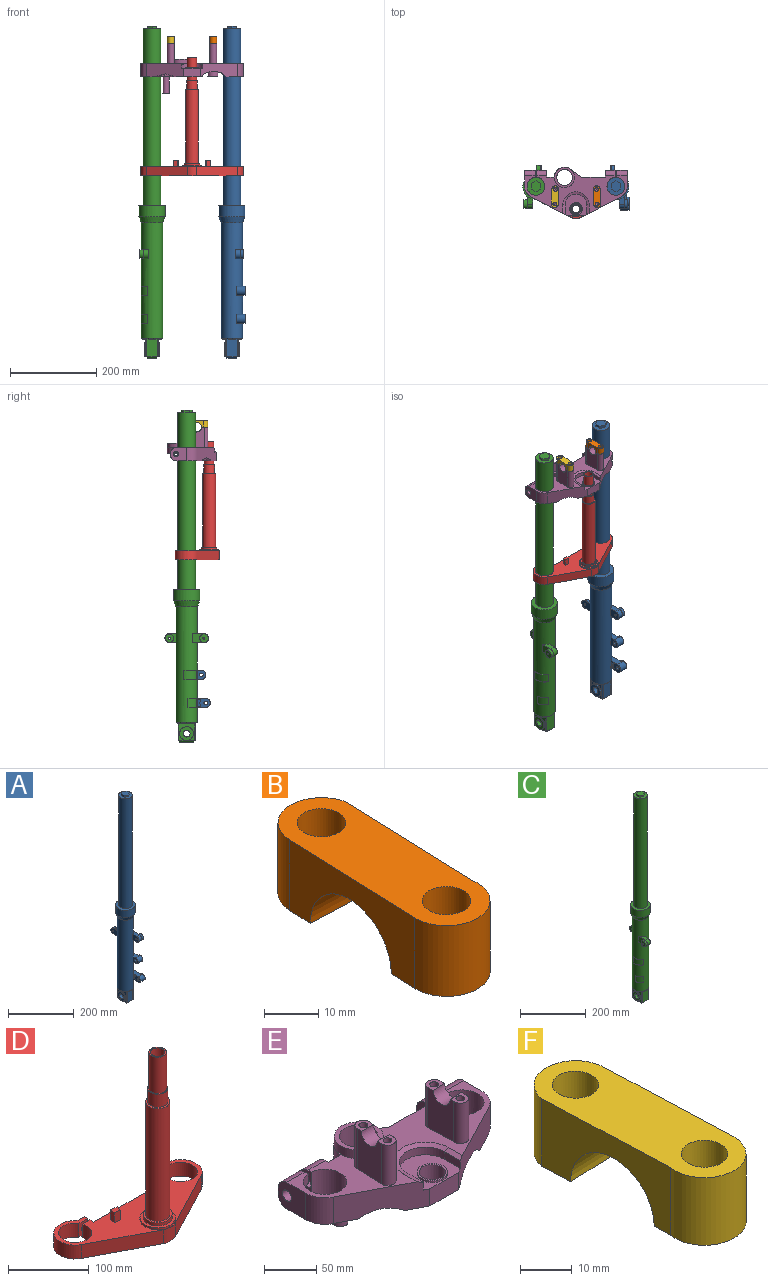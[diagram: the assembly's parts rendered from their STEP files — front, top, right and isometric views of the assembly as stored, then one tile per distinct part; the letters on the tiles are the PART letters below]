
ASSEMBLY  parts=6 mates=5
PART A: 81 faces, bbox 60.9x105.3x769.3 mm
  f0: cylinder r=10.5mm len=21mm, axis (1,0,0), area 824.7mm2, adj f15,f17,f32,f78,f80
  f1: cylinder r=10.5mm len=21mm, axis (1,0,0), area 824.7mm2, adj f2,f27,f29,f30,f46
  f2: plane 21x21mm, normal (1,0,0), area 291.3mm2, adj f1,f3
  f3: cylinder r=4.19mm len=20mm, axis (1,0,0), area 526.3mm2, adj f2,f30
  f4: cylinder r=2.46mm len=10.25mm, axis (-1,0,0), area 158.3mm2, adj f5,f6
  f5: plane 19x19mm, normal (1,0,0), area 264.5mm2, adj f4,f7
  f6: plane 28.95x21mm, normal (-1,0,0), area 541.7mm2, adj f4,f8,f9,f10,f11
  f7: cylinder r=9.5mm len=19mm, axis (-1,0,0), area 447.7mm2, adj f5,f12
  f8: plane 18.45x2.75mm, normal (0,0,-1), area 48.7mm2, adj f6,f9,f11,f12
  f9: cylinder r=10.5mm len=21mm, axis (1,0,0), area 90.7mm2, adj f6,f8,f10,f12
  f10: plane 18.45x2.75mm, normal (0,0,1), area 48.7mm2, adj f6,f9,f11,f12
  f11: cylinder r=24.65mm len=267mm, axis (0,0,-1), area 39688.9mm2, adj f6,f8,f10,f12,f13,f14,f15,f16
  f12: plane 27.57x21mm, normal (1,0,0), area 248.1mm2, adj f7,f8,f9,f10,f11
  f13: cone r=1mm half-angle=45deg, axis (0,0,1), area 565.9mm2, adj f11,f18,f19,f20,f21,f22,f33,f34
  f14: plane 50.5x50.5mm, normal (0,0,-1), area 94.1mm2, adj f11,f31
  f15: plane 41.27x15mm, normal (0,0,1), area 291mm2, adj f0,f11,f16,f32,f78
  f16: plane 21x1.71mm, normal (0,1,0), area 36mm2, adj f11,f15,f17,f32
  f17: plane 41.27x15mm, normal (0,0,-1), area 291mm2, adj f0,f11,f16,f32,f78
  f18: plane 42.22x25.29mm, normal (0,1,0), area 1007.7mm2, adj f13,f19,f22,f33,f37
  f19: plane 16.58x1.65mm, normal (0,0,-1), area 18.4mm2, adj f13,f18
  f20: plane 32.15x7.15mm, normal (0,0,-1), area 159.2mm2, adj f13,f21
  f21: plane 41.54x36.07mm, normal (-1,0,0), area 638.5mm2, adj f13,f20,f22,f38,f39,f40
  f22: cylinder r=2mm len=42.52mm, axis (0,0,-1), area 131.9mm2, adj f13,f18,f21,f37,f39
  f23: plane 26.33x12.5mm, normal (0,0,1), area 256.6mm2, adj f11,f24,f26,f43
  f24: plane 36.83x21mm, normal (1,0,0), area 411.9mm2, adj f11,f23,f25,f43,f44
  f25: plane 26.33x12.5mm, normal (0,0,-1), area 256.6mm2, adj f11,f24,f26,f43
  f26: plane 27.38x21mm, normal (-1,0,0), area 508mm2, adj f11,f23,f25,f43,f45
  f27: plane 41.27x15mm, normal (0,0,1), area 431.5mm2, adj f1,f11,f28,f30,f46
  f28: plane 21x0.87mm, normal (0,1,0), area 18.3mm2, adj f11,f27,f29,f46
  f29: plane 41.27x15mm, normal (0,0,-1), area 431.5mm2, adj f1,f11,f28,f30,f46
  f30: plane 32.37x21mm, normal (-1,0,0), area 485.9mm2, adj f1,f3,f11,f27,f29,f47,f48,f49
  f31: cone r=0.36mm half-angle=20deg, axis (0,0,1), area 2548.9mm2, adj f14,f52
  f32: plane 41.27x21mm, normal (1,0,0), area 693.5mm2, adj f0,f15,f16,f17
  f33: cylinder r=2mm len=42.52mm, axis (0,0,-1), area 131.9mm2, adj f13,f18,f34,f37,f53
  f34: plane 41.54x36.07mm, normal (1,0,0), area 638.5mm2, adj f13,f33,f35,f36,f53,f54
  f35: plane 32.15x7.15mm, normal (0,0,-1), area 159.2mm2, adj f13,f34
  f36: cylinder r=2mm len=42.52mm, axis (0,0,-1), area 131.9mm2, adj f13,f34,f41,f53,f55
  f37: plane 28.09x3.26mm, normal (0,0.71,-0.71), area 109.1mm2, adj f18,f22,f33,f39,f53,f56
  f38: cylinder r=2mm len=42.52mm, axis (0,0,-1), area 131.9mm2, adj f13,f21,f39,f41,f55
  f39: plane 39.09x3.26mm, normal (-0.71,0,-0.71), area 155.8mm2, adj f21,f22,f37,f38,f55,f56
  f40: cylinder r=16mm len=32mm, axis (-1,0,0), area 301.6mm2, adj f21,f57
  f41: plane 42.22x25.29mm, normal (0,-1,0), area 1007.7mm2, adj f13,f36,f38,f42,f55
  f42: plane 16.58x1.65mm, normal (0,0,-1), area 18.4mm2, adj f13,f41
  f43: cylinder r=10.5mm len=21mm, axis (1,0,0), area 412.3mm2, adj f23,f24,f25,f26
  f44: cylinder r=10mm len=20mm, axis (-1,0,0), area 471.2mm2, adj f24,f58
  f45: cylinder r=2.5mm len=20mm, axis (-1,0,0), area 314.2mm2, adj f26,f58
  f46: plane 41.27x21mm, normal (1,0,0), area 693.5mm2, adj f1,f27,f28,f29
  f47: plane 7.65x2.5mm, normal (0,0,1), area 19.1mm2, adj f30,f48,f51,f59
  f48: cylinder r=13.5mm len=7.5mm, axis (-1,0,0), area 19.9mm2, adj f30,f47,f49,f59
  f49: cylinder r=13.5mm len=7.5mm, axis (-1,0,0), area 19.9mm2, adj f30,f48,f50,f59
  f50: plane 7.65x2.5mm, normal (0,0,-1), area 19.1mm2, adj f30,f49,f51,f59
  f51: plane 15x2.5mm, normal (0,-1,0), area 37.5mm2, adj f30,f47,f50,f59
  f52: cylinder r=30.25mm len=60.5mm, axis (0,0,1), area 4991.6mm2, adj f31,f60
  f53: plane 39.09x3.26mm, normal (0.71,0,-0.71), area 155.7mm2, adj f33,f34,f36,f37,f55,f56
  f54: cylinder r=16mm len=32mm, axis (1,0,0), area 301.6mm2, adj f34,f61
  f55: plane 28.09x3.26mm, normal (0,-0.71,-0.71), area 109.1mm2, adj f36,f38,f39,f41,f53,f56
  f56: plane 34x23mm, normal (0,0,-1), area 568.2mm2, adj f37,f39,f53,f55,f62
  f57: plane 32x32mm, normal (-1,0,0), area 603.2mm2, adj f40,f63
  f58: plane 20x20mm, normal (1,0,0), area 294.5mm2, adj f44,f45
  f59: plane 15x7.65mm, normal (-1,0,0), area 91.6mm2, adj f47,f48,f49,f50,f51
  f60: plane 60.5x60.5mm, normal (0,0,1), area 1541.6mm2, adj f52,f64
  f61: plane 32x32mm, normal (1,0,0), area 603.2mm2, adj f54,f65
  f62: cylinder r=8.25mm len=25mm, axis (0,0,-1), area 928.2mm2, adj f56,f63,f65,f66,f67
  f63: cylinder r=8mm len=16mm, axis (-1,0,0), area 595mm2, adj f57,f62,f66,f67,f69
  f64: cylinder r=20.6mm len=410mm, axis (0,0,-1), area 53067.8mm2, adj f60,f68
  f65: cylinder r=8mm len=16.58mm, axis (1,0,0), area 645.2mm2, adj f61,f62,f66,f67,f69
  f66: plane 11.46x2.31mm, normal (0,0,-1), area 13.5mm2, adj f62,f63,f65,f69
  f67: plane 11.96x2.57mm, normal (0,0,-1), area 14.6mm2, adj f62,f63,f65,f69
  f68: plane 41.2x41.2mm, normal (0,0,1), area 914mm2, adj f64,f70,f71,f72,f73,f74,f75
  f69: cylinder r=6.92mm len=43mm, axis (0,0,1), area 1844.4mm2, adj f63,f65,f66,f67,f76
  f70: plane 11x6.35mm, normal (-0.5,0.87,0), area 76.2mm2, adj f68,f71,f75,f77
  f71: plane 12.7x6mm, normal (-1,0,0), area 76.2mm2, adj f68,f70,f72,f77
  f72: plane 11x6.35mm, normal (-0.5,-0.87,0), area 76.2mm2, adj f68,f71,f73,f77
  f73: plane 11x6.35mm, normal (0.5,-0.87,0), area 76.2mm2, adj f68,f72,f74,f77
  f74: plane 12.7x6mm, normal (1,0,0), area 76.2mm2, adj f68,f73,f75,f77
  f75: plane 11x6.35mm, normal (0.5,0.87,0), area 76.2mm2, adj f68,f70,f74,f77
  f76: cone r=1.73mm half-angle=60deg, axis (0,0,-1), area 173.6mm2, adj f69
  f77: plane 25.4x22mm, normal (0,0,1), area 419.2mm2, adj f70,f71,f72,f73,f74,f75
  f78: plane 22.37x21mm, normal (-1,0,0), area 367.4mm2, adj f0,f11,f15,f17,f79
  f79: cylinder r=4.19mm len=20mm, axis (1,0,0), area 526.3mm2, adj f78,f80
  f80: plane 21x21mm, normal (1,0,0), area 291.3mm2, adj f0,f79
PART B: 10 faces, bbox 17.2x50x16 mm
  f0: cylinder r=8.03mm len=16mm, axis (0,0,-1), area 376.8mm2, adj f2,f3,f6,f7
  f1: cylinder r=8.03mm len=16.06mm, axis (0,0,-1), area 430.7mm2, adj f2,f3,f5,f7
  f2: plane 33.98x16mm, normal (1,-0.04,0), area 353.9mm2, adj f0,f1,f4,f5,f6,f7
  f3: plane 33.98x16mm, normal (-1,0.04,0), area 353.9mm2, adj f0,f1,f4,f5,f6,f7
  f4: cylinder r=11mm len=22.59mm, axis (1,-0.04,0), area 549mm2, adj f2,f3,f5,f6
  f5: plane 16.12x14.71mm, normal (0,0,-1), area 139.2mm2, adj f1,f2,f3,f4,f8
  f6: plane 16.15x13.95mm, normal (0,0,-1), area 126.8mm2, adj f0,f2,f3,f4,f9
  f7: plane 50.04x17.23mm, normal (0,0,1), area 615.6mm2, adj f0,f1,f2,f3,f8,f9
  f8: cylinder r=4.5mm len=16mm, axis (0,0,-1), area 452.4mm2, adj f5,f7
  f9: cylinder r=4.5mm len=16mm, axis (0,0,-1), area 452.4mm2, adj f6,f7
PART C: 69 faces, bbox 60.8x101.3x769.3 mm
  f0: cylinder r=2.46mm len=10.25mm, axis (-1,0,0), area 158.3mm2, adj f1,f2
  f1: plane 19x19mm, normal (-1,0,0), area 264.5mm2, adj f0,f3
  f2: plane 28.95x21mm, normal (1,0,0), area 541.7mm2, adj f0,f4,f5,f6,f68
  f3: cylinder r=9.5mm len=19mm, axis (-1,0,0), area 447.7mm2, adj f1,f7
  f4: cylinder r=10.5mm len=21mm, axis (1,0,0), area 90.7mm2, adj f2,f5,f7,f68
  f5: plane 18.45x2.75mm, normal (0,0,1), area 48.7mm2, adj f2,f4,f6,f7
  f6: cylinder r=24.65mm len=267mm, axis (0,0,1), area 39688.9mm2, adj f2,f5,f7,f8,f9,f10,f11,f12
  f7: plane 27.57x21mm, normal (-1,0,0), area 248.1mm2, adj f3,f4,f5,f6,f68
  f8: cone r=1mm half-angle=45deg, axis (0,0,1), area 565.9mm2, adj f6,f13,f14,f15,f16,f17,f27,f28
  f9: plane 50.5x50.5mm, normal (0,0,-1), area 94.1mm2, adj f6,f26
  f10: plane 30.05x14.91mm, normal (0,0,1), area 21.4mm2, adj f6,f11,f18,f65
  f11: plane 21x0.63mm, normal (0,1,0), area 13.1mm2, adj f6,f10,f12,f65
  f12: plane 30.05x14.91mm, normal (0,0,-1), area 21.4mm2, adj f6,f11,f18,f65
  f13: plane 16.58x1.65mm, normal (0,0,-1), area 18.4mm2, adj f8,f14
  f14: plane 42.22x25.29mm, normal (0,1,0), area 1007.7mm2, adj f8,f13,f15,f30,f31
  f15: cylinder r=2mm len=42.52mm, axis (0,0,1), area 131.9mm2, adj f8,f14,f16,f31,f32
  f16: plane 41.54x36.07mm, normal (1,0,0), area 638.5mm2, adj f8,f15,f17,f32,f33,f34
  f17: plane 32.15x7.15mm, normal (0,0,-1), area 159.2mm2, adj f8,f16
  f18: plane 21x0.66mm, normal (1,0,0), area 13.8mm2, adj f6,f10,f12,f65
  f19: plane 27.38x21mm, normal (1,0,0), area 508mm2, adj f6,f21,f37,f38,f67
  f20: plane 36.83x21mm, normal (-1,0,0), area 411.9mm2, adj f6,f21,f37,f39,f67
  f21: plane 26.33x12.5mm, normal (0,0,1), area 256.6mm2, adj f6,f19,f20,f37
  f22: plane 21x0.66mm, normal (1,0,0), area 13.8mm2, adj f6,f23,f25,f66
  f23: plane 20.05x14.73mm, normal (0,0,-1), area 15.3mm2, adj f6,f22,f24,f66
  f24: plane 21x0.6mm, normal (0,1,0), area 12.7mm2, adj f6,f23,f25,f66
  f25: plane 20.05x14.73mm, normal (0,0,1), area 15.3mm2, adj f6,f22,f24,f66
  f26: cone r=0.36mm half-angle=20deg, axis (0,0,1), area 2548.9mm2, adj f9,f40
  f27: cylinder r=2mm len=42.52mm, axis (0,0,1), area 131.9mm2, adj f8,f28,f36,f41,f42
  f28: plane 41.54x36.07mm, normal (-1,0,0), area 638.5mm2, adj f8,f27,f29,f30,f42,f43
  f29: plane 32.15x7.15mm, normal (0,0,-1), area 159.2mm2, adj f8,f28
  f30: cylinder r=2mm len=42.52mm, axis (0,0,1), area 131.9mm2, adj f8,f14,f28,f31,f42
  f31: plane 28.09x3.26mm, normal (0,0.71,-0.71), area 109.1mm2, adj f14,f15,f30,f32,f42,f44
  f32: plane 39.09x3.26mm, normal (0.71,0,-0.71), area 155.8mm2, adj f15,f16,f31,f33,f41,f44
  f33: cylinder r=2mm len=42.52mm, axis (0,0,1), area 131.9mm2, adj f8,f16,f32,f36,f41
  f34: cylinder r=16mm len=32mm, axis (-1,0,0), area 301.6mm2, adj f16,f45
  f35: plane 16.58x1.65mm, normal (0,0,-1), area 18.4mm2, adj f8,f36
  f36: plane 42.22x25.29mm, normal (0,-1,0), area 1007.7mm2, adj f8,f27,f33,f35,f41
  f37: cylinder r=10.5mm len=21mm, axis (1,0,0), area 412.3mm2, adj f19,f20,f21,f67
  f38: cylinder r=2.5mm len=20mm, axis (-1,0,0), area 314.2mm2, adj f19,f46
  f39: cylinder r=10mm len=20mm, axis (-1,0,0), area 471.2mm2, adj f20,f46
  f40: cylinder r=30.25mm len=60.5mm, axis (0,0,-1), area 4991.6mm2, adj f26,f47
  f41: plane 28.09x3.26mm, normal (0,-0.71,-0.71), area 109.1mm2, adj f27,f32,f33,f36,f42,f44
  f42: plane 39.09x3.26mm, normal (-0.71,0,-0.71), area 155.8mm2, adj f27,f28,f30,f31,f41,f44
  f43: cylinder r=16mm len=32mm, axis (1,0,0), area 301.6mm2, adj f28,f48
  f44: plane 34x23mm, normal (0,0,-1), area 568.2mm2, adj f31,f32,f41,f42,f49
  f45: plane 32x32mm, normal (1,0,0), area 603.2mm2, adj f34,f50
  f46: plane 20x20mm, normal (-1,0,0), area 294.5mm2, adj f38,f39
  f47: plane 60.5x60.5mm, normal (0,0,1), area 1541.6mm2, adj f40,f51
  f48: plane 32x32mm, normal (-1,0,0), area 603.2mm2, adj f43,f52
  f49: cylinder r=8.25mm len=25mm, axis (0,0,1), area 928.2mm2, adj f44,f50,f52,f53,f54
  f50: cylinder r=8mm len=16mm, axis (-1,0,0), area 595.3mm2, adj f45,f49,f53,f54,f56
  f51: cylinder r=20.6mm len=410mm, axis (0,0,1), area 53067.8mm2, adj f47,f55
  f52: cylinder r=8mm len=16.58mm, axis (1,0,0), area 645.6mm2, adj f48,f49,f53,f54,f56
  f53: plane 11.46x2.31mm, normal (0,0,-1), area 13.5mm2, adj f49,f50,f52,f56
  f54: plane 11.96x2.57mm, normal (0,0,-1), area 14.6mm2, adj f49,f50,f52,f56
  f55: plane 41.2x41.2mm, normal (0,0,1), area 914mm2, adj f51,f57,f58,f59,f60,f61,f62
  f56: cylinder r=6.92mm len=43mm, axis (0,0,-1), area 1844.4mm2, adj f50,f52,f53,f54,f63
  f57: plane 11x6.35mm, normal (0.5,0.87,0), area 76.2mm2, adj f55,f58,f62,f64
  f58: plane 12.7x6mm, normal (1,0,0), area 76.2mm2, adj f55,f57,f59,f64
  f59: plane 11x6.35mm, normal (0.5,-0.87,0), area 76.2mm2, adj f55,f58,f60,f64
  f60: plane 11x6.35mm, normal (-0.5,-0.87,0), area 76.2mm2, adj f55,f59,f61,f64
  f61: plane 12.7x6mm, normal (-1,0,0), area 76.2mm2, adj f55,f60,f62,f64
  f62: plane 11x6.35mm, normal (-0.5,0.87,0), area 76.2mm2, adj f55,f57,f61,f64
  f63: cone r=1.73mm half-angle=60deg, axis (0,0,-1), area 173.6mm2, adj f56
  f64: plane 25.4x22mm, normal (0,0,1), area 419.2mm2, adj f57,f58,f59,f60,f61,f62
  f65: cylinder r=25.25mm len=30.05mm, axis (0,0,1), area 758.5mm2, adj f10,f11,f12,f18
  f66: cylinder r=25.25mm len=21mm, axis (0,0,1), area 546.4mm2, adj f22,f23,f24,f25
  f67: plane 26.33x12.5mm, normal (0,0,-1), area 256.6mm2, adj f6,f19,f20,f37
  f68: plane 18.45x2.75mm, normal (0,0,-1), area 48.7mm2, adj f2,f4,f6,f7
PART D: 60 faces, bbox 237.9x101.4x275 mm
  f0: plane 15x7.87mm, normal (-0.98,0.18,0), area 120mm2, adj f1,f2,f3,f10
  f1: plane 11.27x9.66mm, normal (0,0,1), area 80mm2, adj f0,f2,f3,f4
  f2: plane 15x9.84mm, normal (-0.18,-0.98,0), area 150mm2, adj f0,f1,f4,f10
  f3: plane 15x9.84mm, normal (0.18,0.98,0), area 150mm2, adj f0,f1,f4,f10
  f4: plane 15x7.87mm, normal (0.98,-0.18,0), area 120mm2, adj f1,f2,f3,f10
  f5: plane 15x9.84mm, normal (0.18,-0.98,0), area 150mm2, adj f6,f7,f8,f10
  f6: plane 11.27x9.66mm, normal (0,0,1), area 80mm2, adj f5,f7,f8,f9
  f7: plane 15x7.87mm, normal (0.98,0.18,0), area 120mm2, adj f5,f6,f9,f10
  f8: plane 15x7.87mm, normal (-0.98,-0.18,0), area 120mm2, adj f5,f6,f9,f10
  f9: plane 15x9.84mm, normal (-0.18,0.98,0), area 150mm2, adj f6,f7,f8,f10
  f10: plane 237.93x101.42mm, normal (0,0,1), area 9052mm2, adj f0,f2,f3,f4,f5,f7,f8,f9
  f11: plane 21x13.06mm, normal (0,1,0), area 219.1mm2, adj f10,f15,f16,f56,f59
  f12: cylinder r=10mm len=13mm, axis (0,0,1), area 105mm2, adj f13,f15,f30,f58,f59
  f13: plane 145.64x41.37mm, normal (0,0,-1), area 4204.6mm2, adj f12,f14,f17,f30,f36,f38,f40,f42
  f14: cylinder r=5mm len=13mm, axis (0,0,1), area 123.2mm2, adj f13,f15,f36,f58
  f15: plane 237.93x101.42mm, normal (0,0,-1), area 6165.6mm2, adj f11,f12,f14,f16,f17,f29,f30,f31
  f16: cylinder r=20.7mm len=41.4mm, axis (0,0,1), area 2637.7mm2, adj f10,f11,f15,f31
  f17: cylinder r=10mm len=13mm, axis (0,0,1), area 107.6mm2, adj f13,f15,f30,f49,f51
  f18: cylinder r=4.5mm len=9mm, axis (0,-1,0), area 169.6mm2, adj f45,f50
  f19: cylinder r=22mm len=44mm, axis (0,0,1), area 414.7mm2, adj f10,f20
  f20: plane 44x44mm, normal (0,0,1), area 502.7mm2, adj f19,f21
  f21: cylinder r=18mm len=36mm, axis (0,0,1), area 565.5mm2, adj f20,f22
  f22: plane 36x36mm, normal (0,0,1), area 311mm2, adj f21,f23
  f23: cylinder r=15mm len=171mm, axis (0,0,1), area 16116.4mm2, adj f22,f24
  f24: plane 30x30mm, normal (0,0,1), area 216mm2, adj f23,f25
  f25: cylinder r=12.5mm len=25mm, axis (0,0,1), area 1570.8mm2, adj f24,f26
  f26: plane 25x25mm, normal (0,0,1), area 110.7mm2, adj f25,f27
  f27: cylinder r=11mm len=55mm, axis (0,0,1), area 3801.3mm2, adj f26,f28
  f28: plane 22x22mm, normal (0,0,1), area 125.7mm2, adj f27,f29
  f29: cylinder r=9mm len=275mm, axis (0,0,1), area 15550.9mm2, adj f15,f28
  f30: plane 114.23x13mm, normal (0,-1,0), area 1485mm2, adj f12,f13,f15,f17
  f31: plane 21x15mm, normal (0,-1,0), area 251.4mm2, adj f10,f15,f16,f32,f33
  f32: cylinder r=4.5mm len=9mm, axis (0,-1,0), area 169.6mm2, adj f31,f34
  f33: plane 21x6mm, normal (1,0,0), area 126mm2, adj f10,f15,f31,f34
  f34: plane 21x12.34mm, normal (0,1,0), area 195.5mm2, adj f10,f15,f32,f33,f35
  f35: cylinder r=26.4mm len=49.82mm, axis (0,0,1), area 1958.6mm2, adj f10,f15,f34,f37
  f36: plane 38.55x20.07mm, normal (0.46,0.89,0), area 565mm2, adj f13,f14,f15,f38
  f37: plane 94.15x49.01mm, normal (-0.46,-0.89,0), area 2228.9mm2, adj f10,f15,f35,f39
  f38: cylinder r=10mm len=13.91mm, axis (0,0,1), area 217.5mm2, adj f13,f15,f36,f40
  f39: cylinder r=22.97mm len=21.21mm, axis (0,0,1), area 463mm2, adj f10,f15,f37,f41
  f40: cylinder r=19mm len=35.33mm, axis (0,0,1), area 589.6mm2, adj f13,f15,f38,f42
  f41: plane 94.15x49.01mm, normal (0.46,-0.89,0), area 2228.9mm2, adj f10,f15,f39,f43
  f42: cylinder r=10mm len=13.91mm, axis (0,0,1), area 217.5mm2, adj f13,f15,f40,f44
  f43: cylinder r=26.4mm len=49.82mm, axis (0,0,1), area 1958.6mm2, adj f10,f15,f41,f45
  f44: plane 38.55x20.07mm, normal (-0.46,0.89,0), area 565mm2, adj f13,f15,f42,f46
  f45: plane 21x12.34mm, normal (0,1,0), area 195.5mm2, adj f10,f15,f18,f43,f47
  f46: cylinder r=5mm len=13mm, axis (0,0,1), area 123.2mm2, adj f13,f15,f44,f49
  f47: plane 21x6mm, normal (-1,0,0), area 126mm2, adj f10,f15,f45,f50
  f48: cone r=1.73mm half-angle=60deg, axis (0,1,0), area 9.2mm2, adj f13,f51
  f49: cylinder r=30.7mm len=13mm, axis (0,0,1), area 73.4mm2, adj f13,f15,f17,f46,f51
  f50: plane 21x15mm, normal (0,-1,0), area 251.4mm2, adj f10,f15,f18,f47,f52
  f51: cylinder r=4.19mm len=30mm, axis (0,-1,0), area 657.3mm2, adj f13,f17,f48,f49,f53
  f52: cylinder r=20.7mm len=41.4mm, axis (0,0,1), area 2637.7mm2, adj f10,f15,f50,f53
  f53: plane 21x13.06mm, normal (0,1,0), area 219.1mm2, adj f10,f15,f51,f52,f54
  f54: plane 21x7mm, normal (-1,0,0), area 147mm2, adj f10,f15,f53,f55
  f55: plane 120.05x21mm, normal (0,1,0), area 2521.1mm2, adj f10,f15,f54,f56
  f56: plane 21x7mm, normal (1,0,0), area 147mm2, adj f10,f11,f15,f55
  f57: cone r=1.73mm half-angle=60deg, axis (0,1,0), area 9.2mm2, adj f13,f59
  f58: cylinder r=30.7mm len=13mm, axis (0,0,1), area 77mm2, adj f12,f13,f14,f15,f59
  f59: cylinder r=4.19mm len=30mm, axis (0,-1,0), area 657.3mm2, adj f11,f12,f13,f57,f58
PART E: 130 faces, bbox 239.5x114.1x117.5 mm
  f0: cylinder r=4.19mm len=30mm, axis (1,0,0), area 610.3mm2, adj f1,f2,f128,f129
  f1: cone r=1.73mm half-angle=60deg, axis (-1,0,0), area 0mm2, adj f0,f2
  f2: plane 30.94x17.32mm, normal (0,1,0), area 529mm2, adj f0,f1,f3,f103,f104,f105,f128
  f3: plane 140.75x59.89mm, normal (0,0,-1), area 2066.4mm2, adj f2,f4,f6,f8,f78,f79,f80,f81
  f4: cylinder r=7.5mm len=38mm, axis (0,0,-1), area 1790.7mm2, adj f3,f5
  f5: plane 15x15mm, normal (0,0,-1), area 176.7mm2, adj f4
  f6: cylinder r=7.5mm len=38mm, axis (0,0,-1), area 1790.7mm2, adj f3,f7
  f7: plane 15x15mm, normal (0,0,-1), area 176.7mm2, adj f6
  f8: cylinder r=41.33mm len=58.2mm, axis (-0.46,-0.89,0), area 512.6mm2, adj f3,f9,f76,f77,f78,f79,f102
  f9: cylinder r=10mm len=15.3mm, axis (0,0,-1), area 195.2mm2, adj f8,f10,f76,f79
  f10: torus R=8mm, axis (0,0,-1), area 52.1mm2, adj f9,f11,f74,f75
  f11: plane 141.86x61.26mm, normal (0,0,-1), area 4565.3mm2, adj f10,f12,f17,f18,f19,f20,f67,f68
  f12: torus R=14mm, axis (0,0,-1), area 251.2mm2, adj f11,f13
  f13: cylinder r=12mm len=24mm, axis (0,0,-1), area 1055.6mm2, adj f12,f14
  f14: plane 24x24mm, normal (0,0,-1), area 225.4mm2, adj f13,f15
  f15: cylinder r=8.5mm len=17mm, axis (0,0,-1), area 854.5mm2, adj f14,f16
  f16: plane 17x17mm, normal (0,0,-1), area 227mm2, adj f15
  f17: torus R=93mm, axis (0,0,-1), area 131.1mm2, adj f11,f18,f73,f82
  f18: torus R=35.3mm, axis (0,0,-1), area 158.7mm2, adj f11,f17,f19,f81
  f19: torus R=23mm, axis (0,0,-1), area 36.7mm2, adj f11,f18,f75,f80
  f20: torus R=8mm, axis (0,0,-1), area 50.5mm2, adj f11,f21,f67,f74
  f21: cylinder r=10mm len=14.12mm, axis (0,0,-1), area 242.8mm2, adj f20,f22,f76,f77
  f22: cylinder r=20.5mm len=38.97mm, axis (0,0,-1), area 720.1mm2, adj f21,f23,f67,f77
  f23: cylinder r=10mm len=14.12mm, axis (0,0,-1), area 178mm2, adj f22,f24,f65,f66,f68,f77
  f24: plane 34.12x17.85mm, normal (-0.46,0.89,0), area 101.4mm2, adj f23,f25,f63,f64,f65,f69
  f25: plane 15.46x12.37mm, normal (0,0,-1), area 111.6mm2, adj f24,f26,f63,f65
  f26: plane 86.58x45.54mm, normal (0.46,-0.89,0), area 2332.6mm2, adj f25,f27,f50,f51,f59,f60,f61,f62
  f27: plane 37.58x7.9mm, normal (-0.67,0,-0.74), area 234.1mm2, adj f26,f28,f43,f62,f63,f64
  f28: cylinder r=23.19mm len=57.92mm, axis (0,1,0), area 508.7mm2, adj f27,f29,f32,f39,f40,f41,f42,f43
  f29: plane 12.37x8.38mm, normal (0,0,-1), area 99.3mm2, adj f28,f30,f31,f42,f84
  f30: plane 22.56x5.49mm, normal (0,-1,0), area 62.3mm2, adj f29,f31,f42,f73,f82
  f31: cylinder r=26.58mm len=19.67mm, axis (0,1,0), area 185.2mm2, adj f29,f30,f82,f83,f84
  f32: plane 21.74x16.17mm, normal (-1,0,0), area 265.2mm2, adj f28,f33,f36,f37,f39,f84,f105
  f33: plane 23x6.9mm, normal (0,1,0), area 158.7mm2, adj f32,f34,f36,f39
  f34: plane 30.9x16.27mm, normal (1,0,0), area 385.8mm2, adj f33,f35,f36,f37,f39,f43,f105
  f35: plane 11.85x9.49mm, normal (0,0,-1), area 72.5mm2, adj f34,f39,f40,f43
  f36: cylinder r=12mm len=23mm, axis (-1,0,0), area 433.5mm2, adj f32,f33,f34,f105
  f37: cylinder r=4.19mm len=30mm, axis (-1,0,0), area 610.3mm2, adj f32,f34,f38,f84
  f38: cone r=1.73mm half-angle=60deg, axis (1,0,0), area 0mm2, adj f37,f84
  f39: cylinder r=12mm len=23mm, axis (-1,0,0), area 314.5mm2, adj f28,f32,f33,f34,f35,f40
  f40: plane 32.57x8.04mm, normal (-0.67,0,-0.74), area 181.9mm2, adj f28,f35,f39,f43
  f41: cylinder r=28.7mm len=20.46mm, axis (0,0,-1), area 92.1mm2, adj f28,f42,f64,f71
  f42: cylinder r=10mm len=10.7mm, axis (0,0,-1), area 42.9mm2, adj f28,f29,f30,f41,f72
  f43: cylinder r=20.7mm len=41.4mm, axis (0,0,-1), area 3725.8mm2, adj f27,f28,f34,f35,f40,f44,f49,f62
  f44: cylinder r=6mm len=24.4mm, axis (1,0,0), area 874.7mm2, adj f43,f45,f49
  f45: plane 36.87x30.9mm, normal (1,0,0), area 964.4mm2, adj f44,f46,f47,f48,f61,f62,f105
  f46: cylinder r=12mm len=24.4mm, axis (-1,0,0), area 459.9mm2, adj f45,f48,f49,f62
  f47: cylinder r=12mm len=24.4mm, axis (-1,0,0), area 459.9mm2, adj f45,f48,f49,f105
  f48: plane 24.4x6.9mm, normal (0,1,0), area 168.4mm2, adj f45,f46,f47,f49
  f49: plane 30.9x16.27mm, normal (-1,0,0), area 337.9mm2, adj f43,f44,f46,f47,f48,f62,f105
  f50: plane 38.3x19.9mm, normal (0,-1,0), area 762.1mm2, adj f26,f51,f77,f102
  f51: plane 50.12x50.01mm, normal (0,0,1), area 1559.5mm2, adj f26,f50,f52,f55,f58,f59,f102
  f52: cylinder r=14.5mm len=29mm, axis (0,0,-1), area 182.2mm2, adj f51,f53
  f53: plane 29x29mm, normal (0,0,1), area 169.6mm2, adj f52,f54
  f54: cylinder r=12.5mm len=25mm, axis (0,0,-1), area 1720mm2, adj f53,f77
  f55: plane 22.07x9mm, normal (1,0,0), area 198.6mm2, adj f51,f56,f58,f102
  f56: plane 22.07x5.5mm, normal (0.34,0,0.94), area 120.7mm2, adj f55,f57,f102,f105
  f57: cone r=2.75mm half-angle=70deg, axis (0,0,1), area 509.8mm2, adj f56,f58,f60,f105
  f58: cylinder r=25mm len=50.01mm, axis (0,0,-1), area 707mm2, adj f51,f55,f57,f59
  f59: plane 22.07x9mm, normal (-1,0,0), area 198.6mm2, adj f26,f51,f58,f60
  f60: plane 22.07x5.5mm, normal (-0.34,0,0.94), area 120.7mm2, adj f26,f57,f59,f105
  f61: cylinder r=26.4mm len=30.9mm, axis (0,0,-1), area 889.9mm2, adj f26,f45,f62,f105
  f62: plane 61.84x40.25mm, normal (0,0,-1), area 735.3mm2, adj f26,f27,f43,f45,f46,f49,f61
  f63: cylinder r=23.19mm len=20.03mm, axis (0,1,0), area 165.2mm2, adj f24,f25,f26,f27,f64
  f64: cylinder r=10mm len=15.3mm, axis (0,0,-1), area 131.5mm2, adj f24,f27,f28,f41,f63,f70
  f65: cylinder r=26.58mm len=19.67mm, axis (0,1,0), area 211.6mm2, adj f23,f24,f25,f26,f66
  f66: plane 17.31x3.37mm, normal (0.74,0,-0.67), area 64.9mm2, adj f23,f26,f65,f77
  f67: torus R=22.5mm, axis (0,0,-1), area 167.3mm2, adj f11,f20,f22,f68
  f68: torus R=8mm, axis (0,0,-1), area 50.5mm2, adj f11,f23,f67,f69
  f69: cylinder r=2mm len=34.87mm, axis (-0.89,-0.46,0), area 120.2mm2, adj f11,f24,f68,f70
  f70: torus R=8mm, axis (0,0,-1), area 52.1mm2, adj f11,f64,f69,f71
  f71: torus R=30.7mm, axis (0,0,-1), area 71.1mm2, adj f11,f41,f70,f72
  f72: torus R=8mm, axis (0,0,-1), area 47.8mm2, adj f11,f42,f71,f73
  f73: cylinder r=2mm len=22.56mm, axis (1,0,0), area 70.5mm2, adj f11,f17,f30,f72
  f74: cylinder r=2mm len=34.87mm, axis (-0.89,0.46,0), area 120.2mm2, adj f10,f11,f20,f76
  f75: torus R=30.7mm, axis (0,0,-1), area 65.2mm2, adj f10,f11,f19,f79
  f76: plane 33.94x17.67mm, normal (0.46,0.89,0), area 361.1mm2, adj f8,f9,f21,f74,f77
  f77: plane 63.59x36.43mm, normal (0,0,-1), area 1065.4mm2, adj f8,f21,f22,f23,f26,f50,f54,f66
  f78: plane 1x0.72mm, normal (-0.46,-0.89,0), area 0.4mm2, adj f3,f8,f79
  f79: cylinder r=28.7mm len=19.63mm, axis (0,0,-1), area 264.6mm2, adj f3,f8,f9,f75,f78,f80
  f80: cylinder r=25mm len=14mm, axis (0,0,-1), area 185.5mm2, adj f3,f19,f79,f81
  f81: cylinder r=33.3mm len=44.97mm, axis (0,0,-1), area 694.4mm2, adj f3,f18,f80,f82
  f82: cylinder r=95mm len=37.55mm, axis (0,0,-1), area 544.4mm2, adj f3,f17,f30,f31,f81,f83
  f83: plane 10.83x3.17mm, normal (0.74,0,-0.67), area 44.2mm2, adj f3,f31,f82,f84
  f84: plane 53.81x30.94mm, normal (0,1,0), area 1205.1mm2, adj f3,f28,f29,f31,f32,f37,f38,f83
  f85: plane 26.21x19.2mm, normal (0.59,0.81,0), area 484mm2, adj f84,f86,f104,f105
  f86: plane 64.07x47.6mm, normal (0,0,-1), area 859.9mm2, adj f85,f87,f90,f103,f104
  f87: cylinder r=18.3mm len=36.6mm, axis (0,0,-1), area 2863.1mm2, adj f86,f88
  f88: plane 46.6x46.6mm, normal (0,0,1), area 653.5mm2, adj f87,f89
  f89: cylinder r=23.3mm len=46.6mm, axis (0,0,-1), area 1464mm2, adj f88,f105
  f90: plane 16.51x16mm, normal (-0.09,1,0), area 265.2mm2, adj f3,f84,f86,f103
  f91: cylinder r=12mm len=23mm, axis (-1,0,0), area 433.5mm2, adj f3,f92,f128,f129
  f92: plane 23x6.9mm, normal (0,1,0), area 158.7mm2, adj f91,f93,f128,f129
  f93: cylinder r=12mm len=23mm, axis (-1,0,0), area 433.5mm2, adj f92,f105,f128,f129
  f94: cylinder r=20.7mm len=41.4mm, axis (0,0,-1), area 3851.7mm2, adj f3,f95,f96,f105,f129
  f95: cylinder r=6mm len=24.4mm, axis (1,0,0), area 874.7mm2, adj f94,f96,f100
  f96: plane 30.9x16.27mm, normal (1,0,0), area 337.9mm2, adj f3,f94,f95,f97,f98,f99,f105
  f97: cylinder r=12mm len=24.4mm, axis (-1,0,0), area 459.9mm2, adj f96,f98,f100,f105
  f98: plane 24.4x6.9mm, normal (0,1,0), area 168.4mm2, adj f96,f97,f99,f100
  f99: cylinder r=12mm len=24.4mm, axis (-1,0,0), area 459.9mm2, adj f3,f96,f98,f100
  f100: plane 36.87x30.9mm, normal (-1,0,0), area 964.4mm2, adj f3,f95,f97,f98,f99,f101,f105
  f101: cylinder r=26.4mm len=30.9mm, axis (0,0,-1), area 889.9mm2, adj f3,f100,f102,f105
  f102: plane 85.6x44.56mm, normal (-0.46,-0.89,0), area 2687.5mm2, adj f3,f8,f50,f51,f55,f56,f77,f101
  f103: cylinder r=23.8mm len=47.56mm, axis (0,0,-1), area 1173.5mm2, adj f2,f3,f86,f90
  f104: cylinder r=23.8mm len=37.87mm, axis (0,0,-1), area 781.3mm2, adj f2,f85,f86,f105
  f105: plane 237.93x106.57mm, normal (0,0,1), area 8423.6mm2, adj f2,f26,f32,f34,f36,f43,f45,f47
  f106: plane 47x33.98mm, normal (1,-0.04,0), area 1407.9mm2, adj f105,f107,f108,f111,f114,f116
  f107: cylinder r=11mm len=22.59mm, axis (-1,0.04,0), area 549mm2, adj f106,f108,f111,f115
  f108: plane 16.17x14.32mm, normal (0,0,1), area 141.4mm2, adj f106,f107,f109,f114,f115
  f109: cylinder r=4.19mm len=30mm, axis (0,0,-1), area 789.4mm2, adj f108,f110
  f110: cone r=1.73mm half-angle=60deg, axis (0,0,1), area 63.6mm2, adj f109
  f111: plane 16.11x14.33mm, normal (0,0,1), area 141.7mm2, adj f106,f107,f112,f115,f116
  f112: cylinder r=4.19mm len=30mm, axis (0,0,-1), area 789.4mm2, adj f111,f113
  f113: cone r=1.73mm half-angle=60deg, axis (0,0,1), area 63.6mm2, adj f112
  f114: cylinder r=8.03mm len=47mm, axis (0,0,-1), area 1106.8mm2, adj f105,f106,f108,f115
  f115: plane 47x33.98mm, normal (-1,0.04,0), area 1407.9mm2, adj f105,f107,f108,f111,f114,f116
  f116: cylinder r=8.03mm len=47mm, axis (0,0,-1), area 1265mm2, adj f105,f106,f111,f115
  f117: cylinder r=8.03mm len=47mm, axis (0,0,-1), area 1106.8mm2, adj f105,f118,f125,f127
  f118: plane 16.17x14.32mm, normal (0,0,1), area 141.4mm2, adj f117,f119,f121,f125,f127
  f119: cylinder r=4.19mm len=30mm, axis (0,0,-1), area 789.4mm2, adj f118,f120
  f120: cone r=1.73mm half-angle=60deg, axis (0,0,1), area 63.6mm2, adj f119
  f121: cylinder r=11mm len=22.59mm, axis (-1,-0.04,0), area 549mm2, adj f118,f122,f125,f127
  f122: plane 16.11x14.33mm, normal (0,0,1), area 141.7mm2, adj f121,f123,f125,f126,f127
  f123: cylinder r=4.19mm len=30mm, axis (0,0,-1), area 789.4mm2, adj f122,f124
  f124: cone r=1.73mm half-angle=60deg, axis (0,0,1), area 63.6mm2, adj f123
  f125: plane 47x33.98mm, normal (-1,-0.04,0), area 1407.9mm2, adj f105,f117,f118,f121,f122,f126
  f126: cylinder r=8.03mm len=47mm, axis (0,0,-1), area 1265mm2, adj f105,f122,f125,f127
  f127: plane 47x33.98mm, normal (1,0.04,0), area 1407.9mm2, adj f105,f117,f118,f121,f122,f126
  f128: plane 30.9x16.17mm, normal (1,0,0), area 382.8mm2, adj f0,f2,f3,f91,f92,f93,f105
  f129: plane 30.9x16.27mm, normal (-1,0,0), area 385.8mm2, adj f0,f3,f91,f92,f93,f94,f105
PART F: 10 faces, bbox 17.2x50x16 mm
  f0: cylinder r=8.03mm len=16mm, axis (0,0,-1), area 376.8mm2, adj f2,f3,f5,f7
  f1: cylinder r=8.03mm len=16.06mm, axis (0,0,-1), area 430.7mm2, adj f2,f3,f6,f7
  f2: plane 33.98x16mm, normal (-1,-0.04,0), area 353.9mm2, adj f0,f1,f4,f5,f6,f7
  f3: plane 33.98x16mm, normal (1,0.04,0), area 353.9mm2, adj f0,f1,f4,f5,f6,f7
  f4: cylinder r=11mm len=22.59mm, axis (1,0.04,0), area 549mm2, adj f2,f3,f5,f6
  f5: plane 16.17x14.32mm, normal (0,0,-1), area 132.8mm2, adj f0,f2,f3,f4,f9
  f6: plane 16.11x14.33mm, normal (0,0,-1), area 133.2mm2, adj f1,f2,f3,f4,f8
  f7: plane 50.04x17.23mm, normal (0,0,1), area 615.6mm2, adj f0,f1,f2,f3,f8,f9
  f8: cylinder r=4.5mm len=16mm, axis (0,0,-1), area 452.4mm2, adj f6,f7
  f9: cylinder r=4.5mm len=16mm, axis (0,0,-1), area 452.4mm2, adj f5,f7
PLACE A at identity
PLACE B rot(axis=(0,0,1),4.3deg) t=(118.97,0.35,0)mm
PLACE C at identity
PLACE D at identity
PLACE E at identity
PLACE F rot(axis=(0,0,-1),4.3deg) t=(-118.96,0.72,0)mm
MATE fastened A.f13 <-> E.f41  axis (0,0,1) through (92.56,52.05,336.4)mm
MATE fastened B.f4 <-> E.f121  axis (1,0.04,0) through (56.38,28.51,296.4)mm
MATE fastened C.f8 <-> E.f75  axis (0,0,1) through (-92.56,52.05,336.4)mm
MATE fastened D.f16 <-> E.f75  axis (0,0,1) through (-92.56,52.05,10.5)mm
MATE fastened F.f4 <-> E.f107  axis (1,-0.04,0) through (-40.51,27.91,296.4)mm
